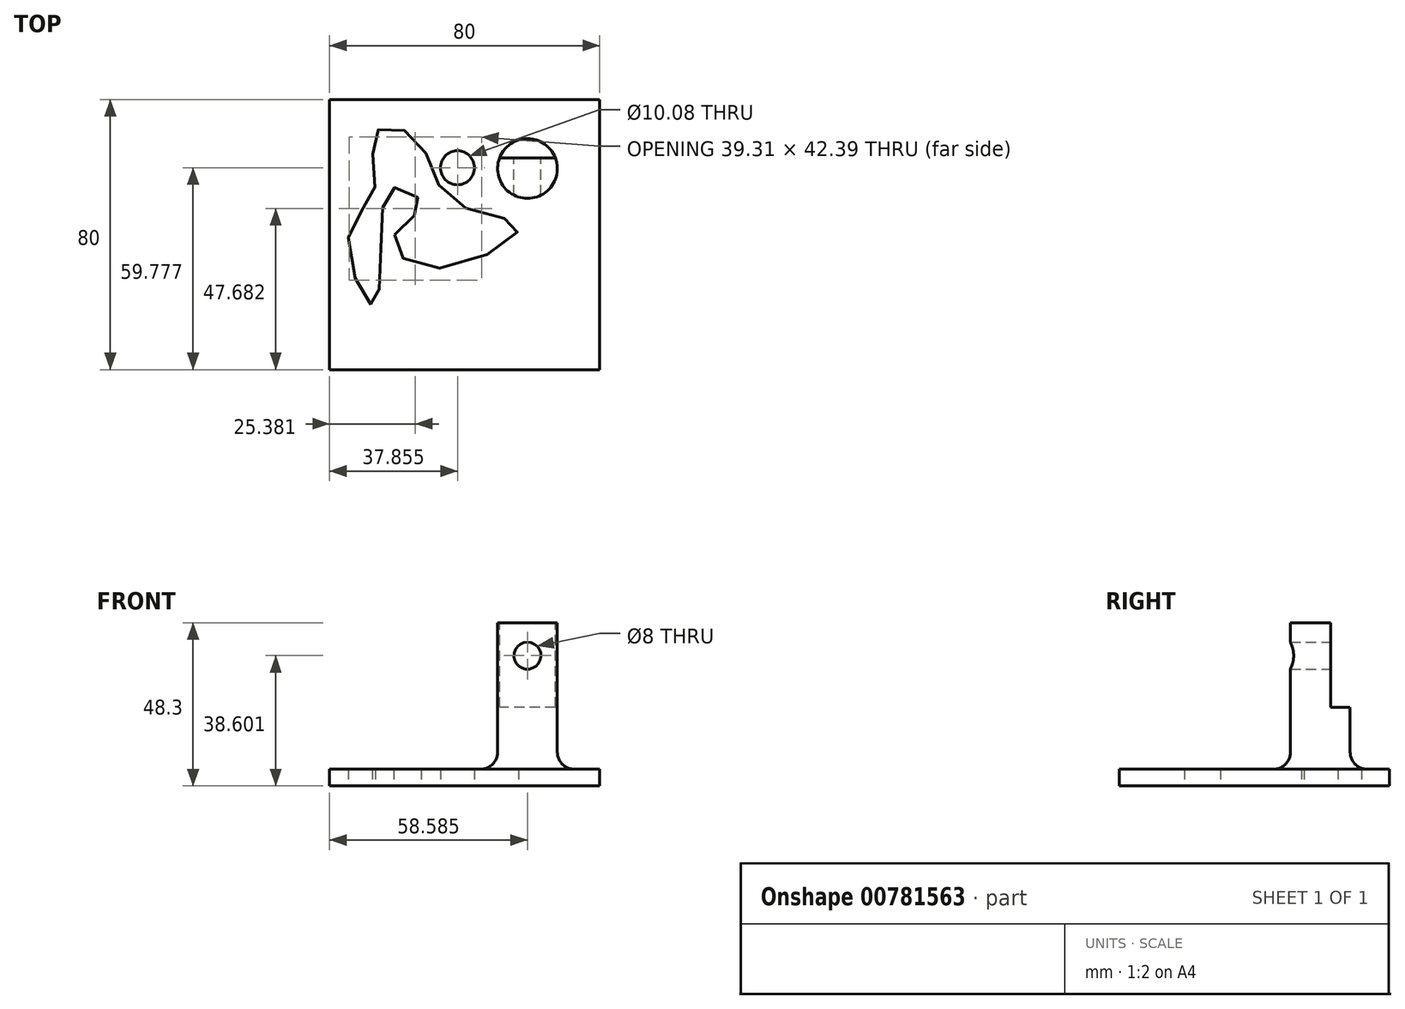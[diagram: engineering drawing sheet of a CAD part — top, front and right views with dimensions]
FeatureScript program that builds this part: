
annotation { "Feature Type Name" : "Feature", "Feature Type Description" : "" }
export const myFeature = defineFeature(function(context is Context, id is Id, definition is map)
    precondition{}
    {
        {
            var Q0;
            Q0=qCreatedBy(makeId("Top.planeOp"),FACE);
            var sketch = newSketch(context, id + "F0", { "sketchPlane" : qUnion([Q0])});
            skLineSegment(sketch, "E0.bottom", {"start": v(40, -40) * mm, "end": v(-40, -40) * mm});
            skLineSegment(sketch, "E0.top", {"start": v(40, 40) * mm, "end": v(-40, 40) * mm});
            skLineSegment(sketch, "E0.left", {"start": v(40, -40) * mm, "end": v(40, 40) * mm});
            skLineSegment(sketch, "E0.right", {"start": v(-40, -40) * mm, "end": v(-40, 40) * mm});
            skPoint(sketch, "E0.middle", {"position": v(0, 0) * mm});
            skSolve(sketch);
        }
        {
            var Q0;
            Q0 = qSketchRegion(id + "F0", true);
            extrude(context, id + "F1", {"entities" : qUnion([Q0]), "depth" : 5 * mm, "offsetDistance" : 25 * mm});
        }
        {
            var Q0;
            Q0=qCreatedBy(makeId("Top.planeOp"),FACE);
            var sketch = newSketch(context, id + "F2", { "sketchPlane" : qUnion([Q0])});
            skPoint(sketch, "E1", {"position": v(-2.14, 19.78) * mm});
            skSolve(sketch);
        }
        {
            var Q0;
            Q0=sQuery(id+"F2.wireOp",VERTEX,"E1");
            var Q1;
            Q1=makeQuery(id+"F1.opExtrude","SWEPT_BODY",BODY,{"disambiguationData":[OSD([sQuery(id+"F0.wireOp",EDGE,"E0.bottom"),sQuery(id+"F0.wireOp",EDGE,"E0.top"),sQuery(id+"F0.wireOp",EDGE,"E0.left"),sQuery(id+"F0.wireOp",EDGE,"E0.right")])]});
            hole(context, id + "F3", {"style" : HoleStyle.SIMPLE, "endStyle" : HoleEndStyle.THROUGH, "oppositeDirection" : true, "standardTappedOrClearance" : lookupTablePath({ "standard" : "ANSI", "fit" : "Normal (ASME)", "size" : "3/8", "type" : "Clearance" }), "standardBlindInLast" : lookupTablePath({ "fit" : "Free", "standard" : "ANSI", "size" : "3/8", "type" : "Clearance" }), "holeDiameter" : 10.08 * mm, "majorDiameter" : 5 * mm, "isTappedThrough" : true, "tappedDepth" : 12 * mm, "tapClearance" : 3, "locations" : qUnion([Q0]), "scope" : qUnion([Q1])});
        }
        {
            var Q0;
            Q0=qCreatedBy(makeId("Top.planeOp"),FACE);
            var sketch = newSketch(context, id + "F4", { "sketchPlane" : qUnion([Q0])});
            skFitSpline(sketch, "E2", {"points": [v(-20.73, 0) * mm, v(-10.72, -10) * mm, v(15.96, 2.14) * mm, v(-3.81, 10) * mm, v(-14.3, 28.35) * mm, v(-26.45, 30.26) * mm, v(-26.69, 13.34) * mm, v(-34.31, 0) * mm, v(-27.64, -20.73) * mm, v(-24.78, -4.77) * mm, v(-20.97, 13.82) * mm, v(-12.87, 8.82) * mm, v(-20.73, 0) * mm]});
            skSolve(sketch);
        }
        {
            var Q0;
            Q0 = qSketchRegion(id + "F4", true);
            extrude(context, id + "F5", {"entities" : qUnion([Q0]), "operationType" : NewBodyOperationType.REMOVE, "depth" : 11.1 * mm, "offsetDistance" : 25 * mm});
        }
        {
            var Q0;
            Q0=qCreatedBy(makeId("Top.planeOp"),FACE);
            var sketch = newSketch(context, id + "F6", { "sketchPlane" : qUnion([Q0])});
            skCircle(sketch, "E3", {"center": v(18.59, 19.54) * mm, "radius": 8.85 * mm});
            skSolve(sketch);
        }
        {
            var Q0;
            Q0 = qSketchRegion(id + "F6", true);
            extrude(context, id + "F7", {"entities" : qUnion([Q0]), "operationType" : NewBodyOperationType.ADD, "depth" : 48.3 * mm, "offsetDistance" : 25 * mm});
        }
        {
            var Q0;
            Q0=makeQuery(id+"F7.boolean.opBoolean","INTERSECT",EDGE,{"derivedFrom":[makeQuery(id+"F1.opExtrude","CAP_FACE",FACE,{"disambiguationData":[OSD([sQuery(id+"F0.wireOp",EDGE,"E0.bottom"),sQuery(id+"F0.wireOp",EDGE,"E0.top"),sQuery(id+"F0.wireOp",EDGE,"E0.left"),sQuery(id+"F0.wireOp",EDGE,"E0.right")])],"isStart":false}),makeQuery(id+"F7.opExtrude","SWEPT_FACE",FACE,{"disambiguationData":[OSD([sQuery(id+"F6.wireOp",EDGE,"E3")])]})]});
            fillet(context, id + "F8", {"entities" : qUnion([Q0]), "radius" : 5 * mm, "tangentPropagation" : true, "allowEdgeOverflow" : false});
        }
        {
            var Q0;
            Q0=makeQuery(id+"F7.opExtrude","CAP_FACE",FACE,{"disambiguationData":[OSD([sQuery(id+"F6.wireOp",EDGE,"E3")])],"isStart":false});
            cPlane(context, id + "F9", {"entities" : qUnion([Q0]), "cplaneType" : CPlaneType.OFFSET, "offset" : 0 * mm, "width" : 150 * mm, "height" : 150 * mm});
        }
        {
            var Q0;
            Q0=qCreatedBy(id+"F9.planeOp",FACE);
            var sketch = newSketch(context, id + "F10", { "sketchPlane" : qUnion([Q0])});
            skCircle(sketch, "E4.0.0", {"center": v(18.59, 19.54) * mm, "radius": 8.85 * mm});
            skLineSegment(sketch, "E5.bottom", {"start": v(33.47, 16.42) * mm, "end": v(3.7, 16.42) * mm});
            skLineSegment(sketch, "E5.top", {"start": v(33.47, 22.66) * mm, "end": v(3.7, 22.66) * mm});
            skLineSegment(sketch, "E5.left", {"start": v(33.47, 16.42) * mm, "end": v(33.47, 22.66) * mm});
            skLineSegment(sketch, "E5.right", {"start": v(3.7, 16.42) * mm, "end": v(3.7, 22.66) * mm});
            skSolve(sketch);
        }
        {
            var Q0;
            {var subQ0=sQuery(id+"F10.wireOp",EDGE,"E5.top");var subQ1=sQuery(id+"F10.wireOp",EDGE,"E4.0.0");var subQ2=makeQuery(id+"F10.imprint","INTERSECT",VERTEX,{"disambiguationData":[OD(0.0)],"derivedFrom":[subQ1,subQ0]});Q0=makeQuery(id+"F10.imprint","IMPRINT",FACE,{"disambiguationData":[TD([[makeQuery(id+"F10.imprint","IMPRINT",EDGE,{"disambiguationData":[TD([[subQ2,-1.0]])],"derivedFrom":subQ1}),1.0]])]});}
            extrude(context, id + "F11", {"entities" : qUnion([Q0]), "operationType" : NewBodyOperationType.REMOVE, "oppositeDirection" : true, "depth" : 25 * mm, "offsetDistance" : 25 * mm});
        }
        {
            var Q0;
            Q0=qCreatedBy(makeId("Front.planeOp"),FACE);
            cPlane(context, id + "F12", {"entities" : qUnion([Q0]), "cplaneType" : CPlaneType.OFFSET, "offset" : 19.8 * mm, "oppositeDirection" : true, "width" : 150 * mm, "height" : 150 * mm});
        }
        {
            var Q0;
            Q0=qCreatedBy(id+"F12.planeOp",FACE);
            var sketch = newSketch(context, id + "F13", { "sketchPlane" : qUnion([Q0])});
            skCircle(sketch, "E6", {"center": v(18.59, 38.6) * mm, "radius": 4 * mm});
            skSolve(sketch);
        }
        {
            var Q0;
            Q0 = qSketchRegion(id + "F13", true);
            extrude(context, id + "F14", {"entities" : qUnion([Q0]), "operationType" : NewBodyOperationType.REMOVE, "depth" : 10 * mm, "offsetDistance" : 25 * mm, "hasSecondDirection" : true, "secondDirectionOppositeDirection" : true, "secondDirectionDepth" : 10 * mm});
        }
    });
